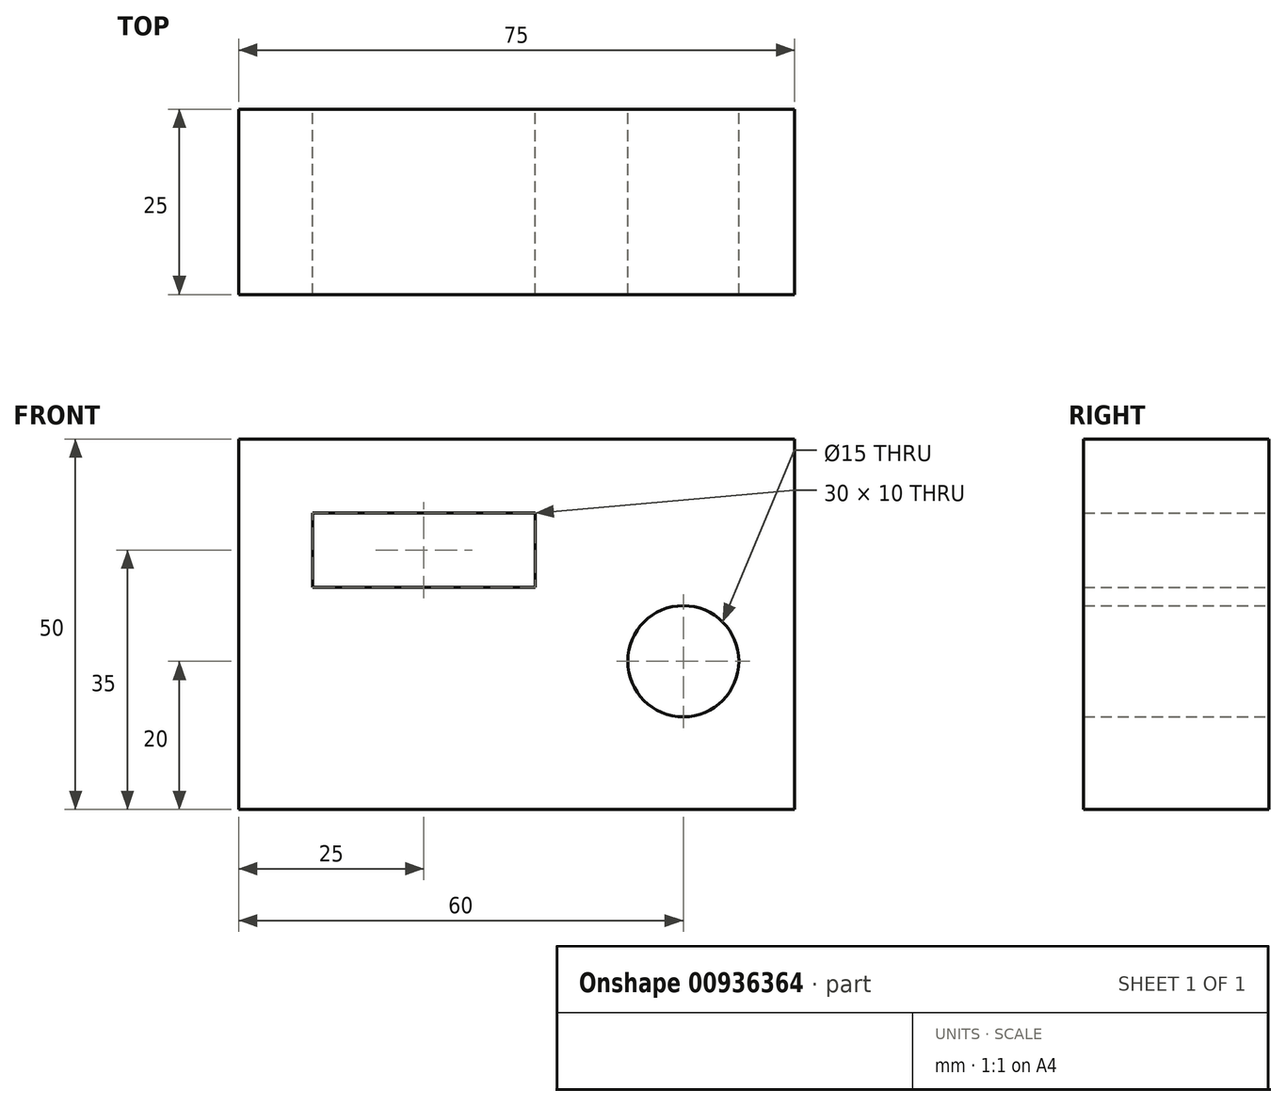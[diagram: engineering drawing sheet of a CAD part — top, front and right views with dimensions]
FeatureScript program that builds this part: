
annotation { "Feature Type Name" : "Feature", "Feature Type Description" : "" }
export const myFeature = defineFeature(function(context is Context, id is Id, definition is map)
    precondition{}
    {
        {
            var Q0;
            Q0=qCreatedBy(makeId("Front.planeOp"),FACE);
            var sketch = newSketch(context, id + "F0", { "sketchPlane" : qUnion([Q0])});
            skLineSegment(sketch, "E0.bottom", {"start": v(-60, 30) * mm, "end": v(15, 30) * mm});
            skLineSegment(sketch, "E0.top", {"start": v(-60, -20) * mm, "end": v(15, -20) * mm});
            skLineSegment(sketch, "E0.left", {"start": v(-60, 30) * mm, "end": v(-60, -20) * mm});
            skLineSegment(sketch, "E0.right", {"start": v(15, 30) * mm, "end": v(15, -20) * mm});
            skCircle(sketch, "E1", {"center": v(0, 0) * mm, "radius": 7.5 * mm});
            skLineSegment(sketch, "E2.bottom", {"start": v(-20, 10) * mm, "end": v(-50, 10) * mm});
            skLineSegment(sketch, "E2.top", {"start": v(-20, 20) * mm, "end": v(-50, 20) * mm});
            skLineSegment(sketch, "E2.left", {"start": v(-20, 10) * mm, "end": v(-20, 20) * mm});
            skLineSegment(sketch, "E2.right", {"start": v(-50, 10) * mm, "end": v(-50, 20) * mm});
            skPoint(sketch, "E2.middle", {"position": v(-35, 15) * mm});
            skSolve(sketch);
        }
        {
            var Q0;
            Q0=makeQuery(id+"F0.imprint","IMPRINT",FACE,{"disambiguationData":[TD([[makeQuery(id+"F0.imprint","IMPRINT",EDGE,{"derivedFrom":sQuery(id+"F0.wireOp",EDGE,"E0.bottom")}),-1.0]])]});
            extrude(context, id + "F1", {"entities" : qUnion([Q0]), "depth" : 25 * mm, "offsetDistance" : 25 * mm});
        }
    });
